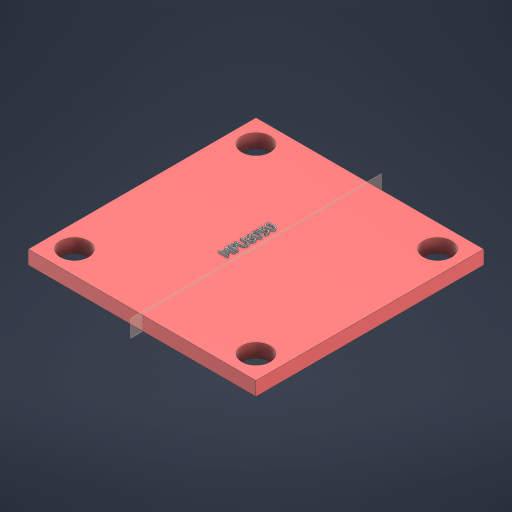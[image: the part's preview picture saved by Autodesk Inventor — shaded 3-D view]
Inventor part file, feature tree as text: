
AUTODESK INVENTOR PART (.ipt)
format: ipt  version: 2023 (Build 270158000, 158)  size: 427,520 bytes
history: native  units: mm
features: sketch x3, extrude x1, hole x1, emboss x1, plane x1
ambient origin geometry x8: Origin, YZ Plane, XZ Plane, XY Plane, X Axis, Y Axis, Z Axis, Center Point
bodies: Solid1 (feature_tree)
feature tree (7):
  extrude  "Extrusion1"  Depth=25.2mm
  hole  "Hole1"  [1 undecoded]
  emboss  "Emboss1"
  plane  "Work Plane1"
  sketch  "Sketch1"  dims[d0=25.2mm d1=25.2mm]
  sketch  "Sketch2"  dims[d2=1.53mm d3=0.0mm d4=2.55mm]
  sketch  "Sketch6"  dims[d5=2.55mm d6=3.1mm d7=6.0mm d8=4.0mm d9=2.0mm d10=90.0deg d11=8.0mm d12=20.594885mm d28=0.2mm d29=0.0mm d30=2.55mm d31=2.55mm]
note: 1 required parameter value undecoded (feature->parameter linkage not recoverable at this tier; creation-order binding heuristic only, values carry confidence <= 0.55)
